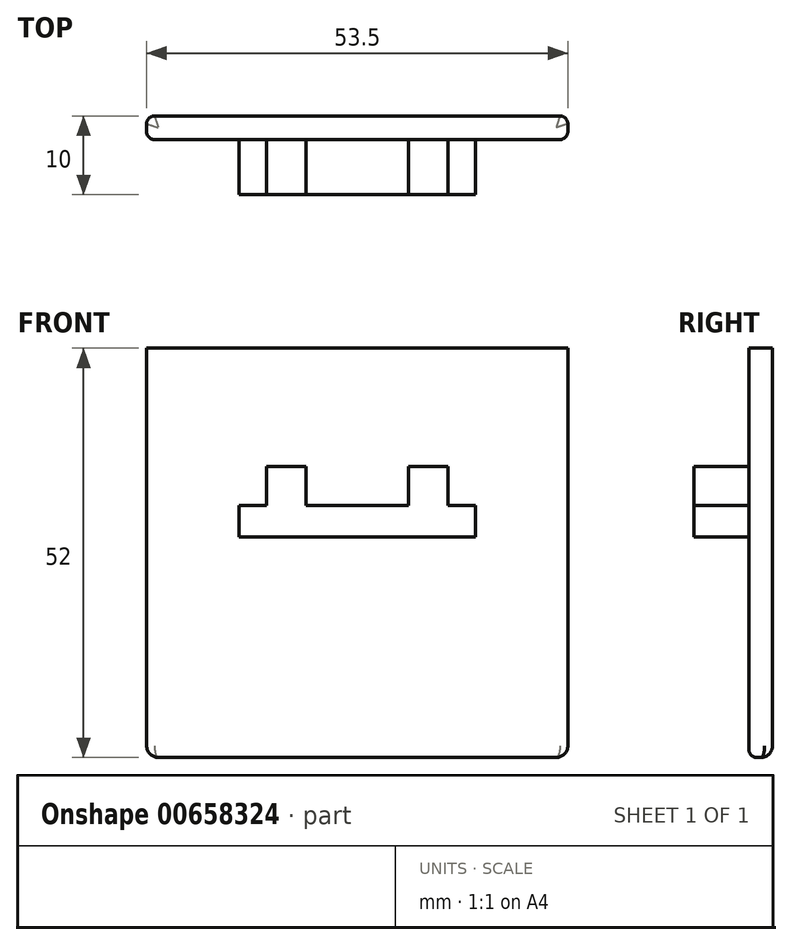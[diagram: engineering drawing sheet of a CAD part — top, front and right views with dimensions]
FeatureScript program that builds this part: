
annotation { "Feature Type Name" : "Feature", "Feature Type Description" : "" }
export const myFeature = defineFeature(function(context is Context, id is Id, definition is map)
    precondition{}
    {
        {
            var Q0;
            Q0=qCreatedBy(makeId("Front.planeOp"),FACE);
            var sketch = newSketch(context, id + "F0", { "sketchPlane" : qUnion([Q0])});
            skLineSegment(sketch, "E0.bottom", {"start": v(0, 0) * mm, "end": v(53.5, 0) * mm});
            skLineSegment(sketch, "E0.top", {"start": v(0, 52) * mm, "end": v(53.5, 52) * mm});
            skLineSegment(sketch, "E0.left", {"start": v(0, 0) * mm, "end": v(0, 52) * mm});
            skLineSegment(sketch, "E0.right", {"start": v(53.5, 0) * mm, "end": v(53.5, 52) * mm});
            skSolve(sketch);
        }
        {
            var Q0;
            Q0 = qSketchRegion(id + "F0", true);
            extrude(context, id + "F1", {"entities" : qUnion([Q0]), "depth" : 3 * mm, "offsetDistance" : 25 * mm});
        }
        {
            var Q0;
            Q0=makeQuery(id+"F1.opExtrude","CAP_FACE",FACE,{"disambiguationData":[OSD([sQuery(id+"F0.wireOp",EDGE,"E0.bottom"),sQuery(id+"F0.wireOp",EDGE,"E0.top"),sQuery(id+"F0.wireOp",EDGE,"E0.left"),sQuery(id+"F0.wireOp",EDGE,"E0.right")])],"isStart":false});
            var sketch = newSketch(context, id + "F2", { "sketchPlane" : qUnion([Q0])});
            skLineSegment(sketch, "E1.bottom", {"start": v(11.75, 32) * mm, "end": v(15.25, 32) * mm});
            skLineSegment(sketch, "E1.top", {"start": v(11.75, 28) * mm, "end": v(41.75, 28) * mm});
            skLineSegment(sketch, "E1.left", {"start": v(11.75, 32) * mm, "end": v(11.75, 28) * mm});
            skLineSegment(sketch, "E1.right", {"start": v(41.75, 32) * mm, "end": v(41.75, 28) * mm});
            skLineSegment(sketch, "E2.top", {"start": v(38.25, 37) * mm, "end": v(33.25, 37) * mm});
            skLineSegment(sketch, "E2.left", {"start": v(38.25, 32) * mm, "end": v(38.25, 37) * mm});
            skLineSegment(sketch, "E2.right", {"start": v(33.25, 32) * mm, "end": v(33.25, 37) * mm});
            skLineSegment(sketch, "E3.top", {"start": v(20.25, 37) * mm, "end": v(15.25, 37) * mm});
            skLineSegment(sketch, "E3.left", {"start": v(20.25, 32) * mm, "end": v(20.25, 37) * mm});
            skLineSegment(sketch, "E3.right", {"start": v(15.25, 32) * mm, "end": v(15.25, 37) * mm});
            skLineSegment(sketch, "E4.trimOffspring", {"start": v(20.25, 32) * mm, "end": v(33.25, 32) * mm});
            skLineSegment(sketch, "E5.trimOffspring", {"start": v(38.25, 32) * mm, "end": v(41.75, 32) * mm});
            skSolve(sketch);
        }
        {
            var Q0;
            Q0 = qSketchRegion(id + "F2", true);
            extrude(context, id + "F3", {"entities" : qUnion([Q0]), "operationType" : NewBodyOperationType.ADD, "depth" : 7 * mm, "offsetDistance" : 25 * mm});
        }
        {
            var Q0;
            Q0=makeQuery(id+"F1.opExtrude","SWEPT_EDGE",EDGE,{"disambiguationData":[OSD([sQuery(id+"F0.wireOp",EDGE,"E0.bottom"),sQuery(id+"F0.wireOp",EDGE,"E0.right")])]});
            var Q1;
            Q1=makeQuery(id+"F1.opExtrude","SWEPT_EDGE",EDGE,{"disambiguationData":[OSD([sQuery(id+"F0.wireOp",EDGE,"E0.bottom"),sQuery(id+"F0.wireOp",EDGE,"E0.left")])]});
            var Q2;
            Q2=makeQuery(id+"F1.opExtrude","CAP_EDGE",EDGE,{"disambiguationData":[OSD([sQuery(id+"F0.wireOp",EDGE,"E0.bottom")])],"isStart":true});
            fillet(context, id + "F4", {"entities" : qUnion([Q0, Q1, Q2]), "radius" : 1.5 * mm, "tangentPropagation" : true, "allowEdgeOverflow" : false});
        }
        {
            var Q0;
            Q0=makeQuery(id+"F1.opExtrude","CAP_EDGE",EDGE,{"disambiguationData":[OSD([sQuery(id+"F0.wireOp",EDGE,"E0.left")])],"isStart":false});
            var Q1;
            Q1=makeQuery(id+"F1.opExtrude","CAP_EDGE",EDGE,{"disambiguationData":[OSD([sQuery(id+"F0.wireOp",EDGE,"E0.right")])],"isStart":false});
            var Q2;
            Q2=makeQuery(id+"F1.opExtrude","CAP_EDGE",EDGE,{"disambiguationData":[OSD([sQuery(id+"F0.wireOp",EDGE,"E0.right")])],"isStart":true});
            var Q3;
            Q3=makeQuery(id+"F1.opExtrude","CAP_EDGE",EDGE,{"disambiguationData":[OSD([sQuery(id+"F0.wireOp",EDGE,"E0.left")])],"isStart":true});
            fillet(context, id + "F5", {"entities" : qUnion([Q0, Q1, Q2, Q3]), "radius" : 1 * mm, "tangentPropagation" : true, "allowEdgeOverflow" : false});
        }
    });
